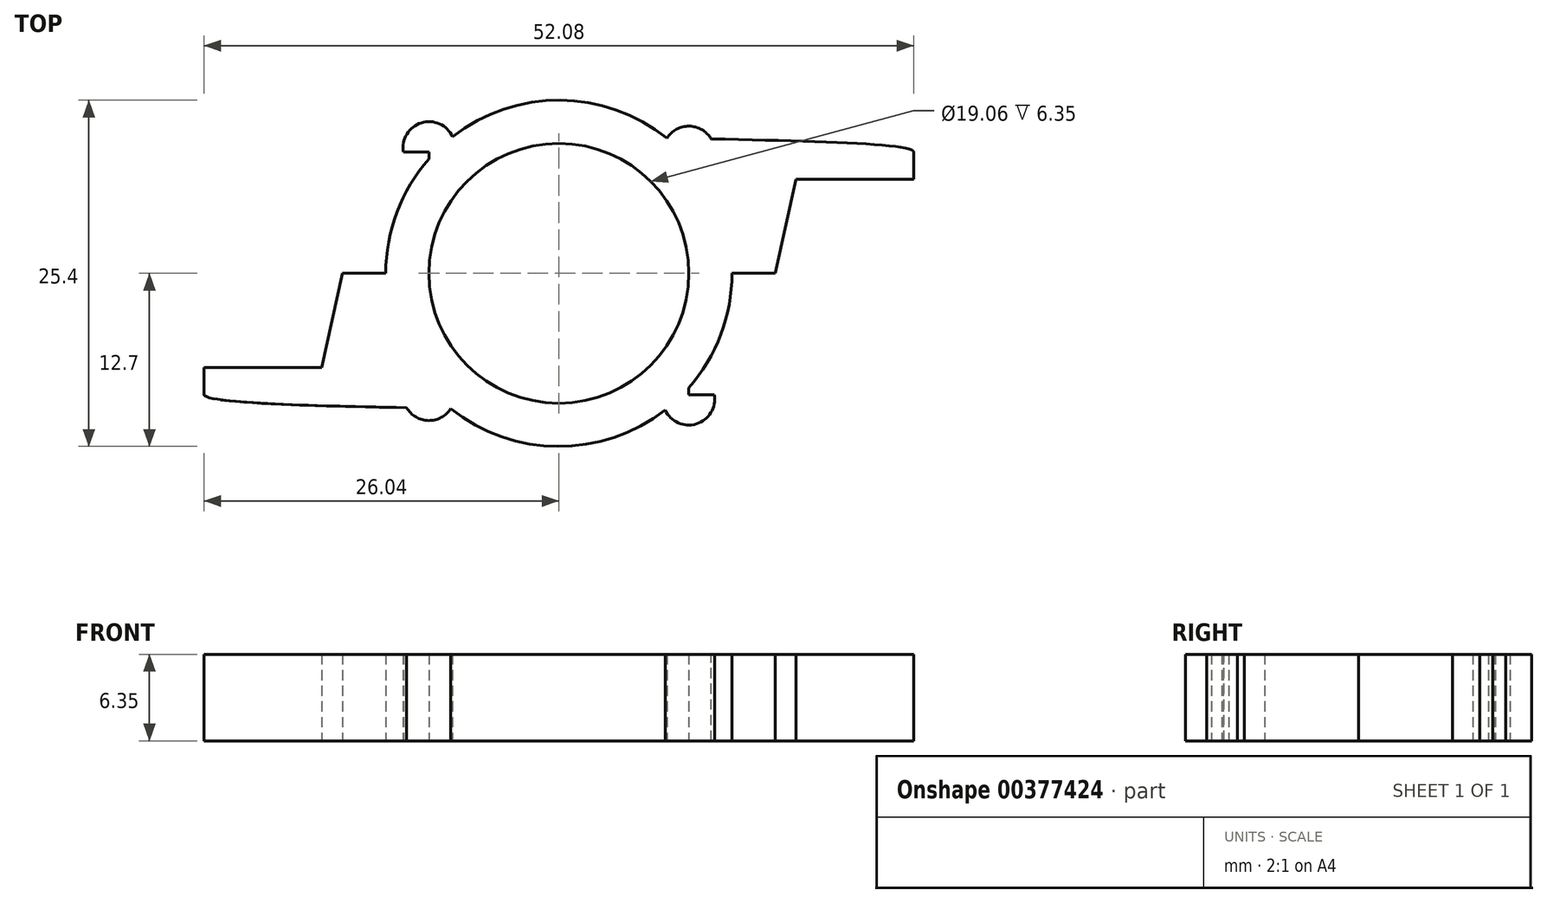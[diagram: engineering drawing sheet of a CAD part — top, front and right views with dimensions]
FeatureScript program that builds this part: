
annotation { "Feature Type Name" : "Feature", "Feature Type Description" : "" }
export const myFeature = defineFeature(function(context is Context, id is Id, definition is map)
    precondition{}
    {
        {
            var Q0;
            Q0=qCreatedBy(makeId("Top.planeOp"),FACE);
            var sketch = newSketch(context, id + "F0", { "sketchPlane" : qUnion([Q0])});
            skCircle(sketch, "E0", {"center": v(0, 0) * mm, "radius": 12.7 * mm});
            skCircle(sketch, "E1", {"center": v(0, 0) * mm, "radius": 9.53 * mm});
            skLineSegment(sketch, "E2", {"start": v(9.53, 0) * mm, "end": v(26.04, 0) * mm});
            skLineSegment(sketch, "E3", {"start": v(26.04, 0) * mm, "end": v(26.04, 8.9) * mm});
            skLineSegment(sketch, "E4", {"start": v(9.53, 0) * mm, "end": v(9.53, -8.9) * mm});
            skLineSegment(sketch, "E5.bottom", {"start": v(9.53, -8.9) * mm, "end": v(26.04, -8.9) * mm});
            skLineSegment(sketch, "E5.top", {"start": v(9.53, 8.9) * mm, "end": v(26.04, 8.9) * mm});
            skLineSegment(sketch, "E5.left", {"start": v(9.53, -8.9) * mm, "end": v(9.53, 8.9) * mm});
            skLineSegment(sketch, "E5.right", {"start": v(26.04, -8.89) * mm, "end": v(26.04, 8.9) * mm});
            skLineSegment(sketch, "E6", {"start": v(26.04, 0) * mm, "end": v(15.88, 0) * mm});
            skPoint(sketch, "E7", {"position": v(26.04, 6.9) * mm});
            skPoint(sketch, "E8", {"position": v(26.04, 0) * mm});
            skPoint(sketch, "E9", {"position": v(26.04, -6.9) * mm});
            skLineSegment(sketch, "E10", {"start": v(26.04, -6.9) * mm, "end": v(17.4, -6.9) * mm});
            skLineSegment(sketch, "E11", {"start": v(26.04, 6.9) * mm, "end": v(17.4, 6.9) * mm});
            skLineSegment(sketch, "E12", {"start": v(17.4, 6.9) * mm, "end": v(15.88, 0) * mm});
            skLineSegment(sketch, "E13", {"start": v(17.4, -6.9) * mm, "end": v(15.88, 0) * mm});
            skCircle(sketch, "E14", {"center": v(9.53, 8.9) * mm, "radius": 1.9 * mm});
            skCircle(sketch, "E15", {"center": v(9.53, -9.23) * mm, "radius": 1.9 * mm});
            skSolve(sketch);
        }
        {
            var Q0;
            {var subQ0=sQuery(id+"F0.wireOp",EDGE,"E14");var subQ1=sQuery(id+"F0.wireOp",EDGE,"E0");var subQ2=makeQuery(id+"F0.imprint","INTERSECT",VERTEX,{"disambiguationData":[OD(1.0)],"derivedFrom":[subQ1,subQ0]});Q0=makeQuery(id+"F0.imprint","IMPRINT",FACE,{"disambiguationData":[TD([[makeQuery(id+"F0.imprint","IMPRINT",EDGE,{"disambiguationData":[TD([[subQ2,1.0]])],"derivedFrom":subQ1}),1.0]])]});}
            var Q1;
            {var subQ0=sQuery(id+"F0.wireOp",EDGE,"E5.left");var subQ1=sQuery(id+"F0.wireOp",EDGE,"E0");var subQ2=makeQuery(id+"F0.imprint","INTERSECT",VERTEX,{"disambiguationData":[OD(1.0)],"derivedFrom":[subQ1,subQ0]});Q1=makeQuery(id+"F0.imprint","IMPRINT",FACE,{"disambiguationData":[TD([[makeQuery(id+"F0.imprint","IMPRINT",EDGE,{"disambiguationData":[TD([[subQ2,-1.0]])],"derivedFrom":subQ1}),1.0]])]});}
            var Q2;
            {var subQ0=sQuery(id+"F0.wireOp",EDGE,"E5.left");var subQ1=sQuery(id+"F0.wireOp",EDGE,"E0");var subQ2=makeQuery(id+"F0.imprint","INTERSECT",VERTEX,{"disambiguationData":[OD(1.0)],"derivedFrom":[subQ1,subQ0]});Q2=makeQuery(id+"F0.imprint","IMPRINT",FACE,{"disambiguationData":[TD([[makeQuery(id+"F0.imprint","IMPRINT",EDGE,{"disambiguationData":[TD([[subQ2,-1.0]])],"derivedFrom":subQ1}),-1.0]])]});}
            var Q3;
            {var subQ0=sQuery(id+"F0.wireOp",EDGE,"E15");var subQ1=sQuery(id+"F0.wireOp",EDGE,"E0");var subQ2=makeQuery(id+"F0.imprint","INTERSECT",VERTEX,{"disambiguationData":[OD(0.0)],"derivedFrom":[subQ1,subQ0]});Q3=makeQuery(id+"F0.imprint","IMPRINT",FACE,{"disambiguationData":[TD([[makeQuery(id+"F0.imprint","IMPRINT",EDGE,{"disambiguationData":[TD([[subQ2,-1.0]])],"derivedFrom":subQ1}),1.0]])]});}
            var Q4;
            {var subQ0=sQuery(id+"F0.wireOp",EDGE,"E14");var subQ1=sQuery(id+"F0.wireOp",EDGE,"E0");var subQ2=makeQuery(id+"F0.imprint","INTERSECT",VERTEX,{"disambiguationData":[OD(0.0)],"derivedFrom":[subQ1,subQ0]});Q4=makeQuery(id+"F0.imprint","IMPRINT",FACE,{"disambiguationData":[TD([[makeQuery(id+"F0.imprint","IMPRINT",EDGE,{"disambiguationData":[TD([[subQ2,1.0]])],"derivedFrom":subQ1}),1.0]])]});}
            var Q5;
            {var subQ3=sQuery(id+"F0.wireOp",EDGE,"E11");Q5=makeQuery(id+"F0.imprint","IMPRINT",FACE,{"disambiguationData":[TD([[makeQuery(id+"F0.imprint","IMPRINT",EDGE,{"derivedFrom":subQ3}),-1.0]])]});}
            var Q6;
            {var subQ0=sQuery(id+"F0.wireOp",EDGE,"E14");var subQ1=sQuery(id+"F0.wireOp",EDGE,"E0");var subQ2=makeQuery(id+"F0.imprint","INTERSECT",VERTEX,{"disambiguationData":[OD(1.0)],"derivedFrom":[subQ1,subQ0]});Q6=makeQuery(id+"F0.imprint","IMPRINT",FACE,{"disambiguationData":[TD([[makeQuery(id+"F0.imprint","IMPRINT",EDGE,{"disambiguationData":[TD([[subQ2,-1.0]])],"derivedFrom":subQ1}),1.0]])]});}
            var Q7;
            {var subQ0=sQuery(id+"F0.wireOp",EDGE,"E14");var subQ1=sQuery(id+"F0.wireOp",EDGE,"E0");var subQ2=makeQuery(id+"F0.imprint","INTERSECT",VERTEX,{"disambiguationData":[OD(1.0)],"derivedFrom":[subQ1,subQ0]});Q7=makeQuery(id+"F0.imprint","IMPRINT",FACE,{"disambiguationData":[TD([[makeQuery(id+"F0.imprint","IMPRINT",EDGE,{"disambiguationData":[TD([[subQ2,-1.0]])],"derivedFrom":subQ1}),-1.0]])]});}
            var Q8;
            {var subQ0=sQuery(id+"F0.wireOp",EDGE,"E15");var subQ1=sQuery(id+"F0.wireOp",EDGE,"E0");var subQ2=makeQuery(id+"F0.imprint","INTERSECT",VERTEX,{"disambiguationData":[OD(0.0)],"derivedFrom":[subQ1,subQ0]});Q8=makeQuery(id+"F0.imprint","IMPRINT",FACE,{"disambiguationData":[TD([[makeQuery(id+"F0.imprint","IMPRINT",EDGE,{"disambiguationData":[TD([[subQ2,-1.0]])],"derivedFrom":subQ1}),-1.0]])]});}
            var Q9;
            {var subQ0=sQuery(id+"F0.wireOp",EDGE,"E14");var subQ1=sQuery(id+"F0.wireOp",EDGE,"E0");var subQ2=makeQuery(id+"F0.imprint","INTERSECT",VERTEX,{"disambiguationData":[OD(0.0)],"derivedFrom":[subQ1,subQ0]});Q9=makeQuery(id+"F0.imprint","IMPRINT",FACE,{"disambiguationData":[TD([[makeQuery(id+"F0.imprint","IMPRINT",EDGE,{"disambiguationData":[TD([[subQ2,1.0]])],"derivedFrom":subQ1}),-1.0]])]});}
            var Q10;
            {var subQ3=sQuery(id+"F0.wireOp",EDGE,"E10");Q10=makeQuery(id+"F0.imprint","IMPRINT",FACE,{"disambiguationData":[TD([[makeQuery(id+"F0.imprint","IMPRINT",EDGE,{"derivedFrom":subQ3}),1.0]])]});}
            var Q11;
            {var subQ0=sQuery(id+"F0.wireOp",EDGE,"E2");var subQ1=sQuery(id+"F0.wireOp",EDGE,"E0");var subQ2=makeQuery(id+"F0.imprint","INTERSECT",VERTEX,{"derivedFrom":[subQ1,subQ0]});Q11=makeQuery(id+"F0.imprint","IMPRINT",FACE,{"disambiguationData":[TD([[makeQuery(id+"F0.imprint","IMPRINT",EDGE,{"disambiguationData":[TD([[subQ2,1.0]])],"derivedFrom":subQ1}),1.0]])]});}
            var Q12;
            {var subQ1=sQuery(id+"F0.wireOp",EDGE,"E1");Q12=makeQuery(id+"F0.imprint","IMPRINT",FACE,{"disambiguationData":[TD([[makeQuery(id+"F0.imprint","IMPRINT",EDGE,{"derivedFrom":subQ1}),-1.0]])]});}
            extrude(context, id + "F1", {"entities" : qUnion([Q0, Q1, Q2, Q3, Q4, Q5, Q6, Q7, Q8, Q9, Q10, Q11, Q12]), "depth" : 6.35 * mm});
        }
        {
            var Q0;
            Q0=qCreatedBy(makeId("Front.planeOp"),FACE);
            var sketch = newSketch(context, id + "F2", { "sketchPlane" : qUnion([Q0])});
            skLineSegment(sketch, "E16", {"start": v(0, 0) * mm, "end": v(0, 6.35) * mm});
            skSolve(sketch);
        }
        {
            var Q0;
            Q0=makeQuery(id+"F1.opExtrude","SWEPT_BODY",BODY,{"disambiguationData":[OSD([sQuery(id+"F0.wireOp",EDGE,"E0"),sQuery(id+"F0.wireOp",EDGE,"E1"),sQuery(id+"F0.wireOp",EDGE,"E5.bottom"),sQuery(id+"F0.wireOp",EDGE,"E5.top"),sQuery(id+"F0.wireOp",EDGE,"E5.right"),sQuery(id+"F0.wireOp",EDGE,"E10"),sQuery(id+"F0.wireOp",EDGE,"E11"),sQuery(id+"F0.wireOp",EDGE,"E12"),sQuery(id+"F0.wireOp",EDGE,"E13"),sQuery(id+"F0.wireOp",EDGE,"E14"),sQuery(id+"F0.wireOp",EDGE,"E15")])]});
            var Q1;
            Q1=sQuery(id+"F2.wireOp",EDGE,"E16");
            circularPattern(context, id + "F3", {"entities" : qUnion([Q0]), "axis" : qUnion([Q1]), "angle" : 360 * degree, "instanceCount" : 2, "equalSpace" : true});
        }
        {
            var Q0;
            Q0=makeQuery(id+"F3.opPattern","COPY",FACE,{"derivedFrom":makeQuery(id+"F1.opExtrude","CAP_FACE",FACE,{"disambiguationData":[OSD([sQuery(id+"F0.wireOp",EDGE,"E0"),sQuery(id+"F0.wireOp",EDGE,"E1"),sQuery(id+"F0.wireOp",EDGE,"E5.bottom"),sQuery(id+"F0.wireOp",EDGE,"E5.top"),sQuery(id+"F0.wireOp",EDGE,"E5.right"),sQuery(id+"F0.wireOp",EDGE,"E10"),sQuery(id+"F0.wireOp",EDGE,"E11"),sQuery(id+"F0.wireOp",EDGE,"E12"),sQuery(id+"F0.wireOp",EDGE,"E13"),sQuery(id+"F0.wireOp",EDGE,"E14"),sQuery(id+"F0.wireOp",EDGE,"E15")])],"isStart":false}),"instanceName":"1"});
            var sketch = newSketch(context, id + "F4", { "sketchPlane" : qUnion([Q0])});
            skFitSpline(sketch, "E17", {"points": [v(-7.8, 10.03) * mm, v(-26.04, 8.9) * mm, v(-17.4, 6.9) * mm], "startDerivative": vector(-46.26, -1.08) * mm, "endDerivative": vector(31.7, -5.42) * mm});
            skFitSpline(sketch, "E18", {"points": [v(-7.92, -9.92) * mm, v(-26.04, -8.89) * mm, v(-17.4, -6.9) * mm], "startDerivative": vector(-46, 0.86) * mm, "endDerivative": vector(31.64, 5.45) * mm});
            skSolve(sketch);
        }
        {
            var Q0;
            {var subQ2=sQuery(id+"F0.wireOp",EDGE,"E5.bottom");var subQ3=makeQuery(id+"F3.opPattern","COPY",EDGE,{"derivedFrom":makeQuery(id+"F1.opExtrude","CAP_EDGE",EDGE,{"disambiguationData":[OSD([subQ2])],"isStart":false}),"instanceName":"1"});Q0=makeQuery(id+"F4.imprint","IMPRINT",FACE,{"disambiguationData":[TD([[makeQuery(id+"F4.imprint","IMPRINT",EDGE,{"derivedFrom":subQ3}),-1.0]])]});}
            var Q1;
            {var subQ2=sQuery(id+"F0.wireOp",EDGE,"E5.top");var subQ3=makeQuery(id+"F3.opPattern","COPY",EDGE,{"derivedFrom":makeQuery(id+"F1.opExtrude","CAP_EDGE",EDGE,{"disambiguationData":[OSD([subQ2])],"isStart":false}),"instanceName":"1"});Q1=makeQuery(id+"F4.imprint","IMPRINT",FACE,{"disambiguationData":[TD([[makeQuery(id+"F4.imprint","IMPRINT",EDGE,{"derivedFrom":subQ3}),1.0]])]});}
            extrude(context, id + "F5", {"entities" : qUnion([Q0, Q1]), "operationType" : NewBodyOperationType.ADD, "oppositeDirection" : true, "depth" : 6.35 * mm});
        }
        {
            var Q0;
            Q0=makeQuery(id+"F1.opExtrude","CAP_FACE",FACE,{"disambiguationData":[OSD([sQuery(id+"F0.wireOp",EDGE,"E0"),sQuery(id+"F0.wireOp",EDGE,"E1"),sQuery(id+"F0.wireOp",EDGE,"E5.bottom"),sQuery(id+"F0.wireOp",EDGE,"E5.top"),sQuery(id+"F0.wireOp",EDGE,"E5.right"),sQuery(id+"F0.wireOp",EDGE,"E10"),sQuery(id+"F0.wireOp",EDGE,"E11"),sQuery(id+"F0.wireOp",EDGE,"E12"),sQuery(id+"F0.wireOp",EDGE,"E13"),sQuery(id+"F0.wireOp",EDGE,"E14"),sQuery(id+"F0.wireOp",EDGE,"E15")])],"isStart":false});
            var sketch = newSketch(context, id + "F6", { "sketchPlane" : qUnion([Q0])});
            skFitSpline(sketch, "E19", {"points": [v(7.92, 9.92) * mm, v(26.04, 8.9) * mm, v(17.4, 6.9) * mm], "startDerivative": vector(46, -0.86) * mm, "endDerivative": vector(-31.64, -5.45) * mm});
            skFitSpline(sketch, "E20", {"points": [v(7.8, -10.03) * mm, v(26.04, -8.9) * mm, v(17.4, -6.9) * mm], "startDerivative": vector(46.26, 1.08) * mm, "endDerivative": vector(-31.7, 5.42) * mm});
            skSolve(sketch);
        }
        {
            var Q0;
            {var subQ2=sQuery(id+"F0.wireOp",EDGE,"E5.top");var subQ3=makeQuery(id+"F1.opExtrude","CAP_EDGE",EDGE,{"disambiguationData":[OSD([subQ2])],"isStart":false});Q0=makeQuery(id+"F6.imprint","IMPRINT",FACE,{"disambiguationData":[TD([[makeQuery(id+"F6.imprint","IMPRINT",EDGE,{"derivedFrom":subQ3}),1.0]])]});}
            var Q1;
            {var subQ2=sQuery(id+"F0.wireOp",EDGE,"E5.bottom");var subQ3=makeQuery(id+"F1.opExtrude","CAP_EDGE",EDGE,{"disambiguationData":[OSD([subQ2])],"isStart":false});Q1=makeQuery(id+"F6.imprint","IMPRINT",FACE,{"disambiguationData":[TD([[makeQuery(id+"F6.imprint","IMPRINT",EDGE,{"derivedFrom":subQ3}),-1.0]])]});}
            extrude(context, id + "F7", {"entities" : qUnion([Q0, Q1]), "operationType" : NewBodyOperationType.ADD, "oppositeDirection" : true, "depth" : 6.35 * mm});
        }
    });
